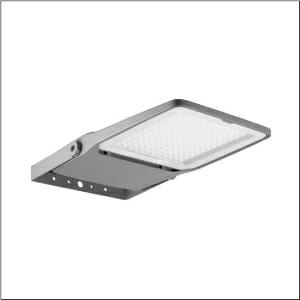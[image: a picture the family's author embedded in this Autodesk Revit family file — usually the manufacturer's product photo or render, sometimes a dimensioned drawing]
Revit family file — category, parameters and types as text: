
# Revit family: floodlight_fl_20_midi___rs17_5xa7682d2b2ac_2315
name_source: partatom
category: Lighting Fixtures
units: mm (PartAtom-declared; Revit-internal decimal feet)

## family parameters
Cut with Voids When Loaded = No
Host = Face
Light Source = No
Part Type = Normal
Room Calculation Point = No
Round Connector Dimension = Use Diameter
Shared = No

## types (1)
- --- (1 x LED 4000K / CRI = 70 (unbekannt), 19540 lm, 4000K)
    Apparent Load = 142 VA
    CIE Flux Codes = 79 92 99 100 100
    Color Rendering = 70
    Color Temperature = 4000K
    Default Elevation = 1800 mm
    Description = Floodlight FL 20 midi, floodlight, primary light control with lens, of plastic, primary optical cover: protective disc, of toughened safety glass, transparent, light distribution: RS17, light emission: direct distribution, primary light characteristic: rotationally symmetric, installation type: surface-mounted, LED, High Power LED, rated luminous flux: 19.540lm, luminous efficacy: 138lm/W, light colour: 740, colour temperature: 4000K, control gear: ECG Plus, control: flexible luminous flux parameterisation, time-dependent luminous flux control, digital communication interface, power reduction, overheat protection, electronic power reduction, with terminal, 5-pole, max. 2.5mm², mains connection: 220..240V, AC, 50/60Hz, rated input power: 142W, LED unit, of diecast aluminium, powder-coated, Siteco® metallic grey (DB 702S), corrosivity category C5 mid according to DIN EN ISO 12944, incl. 1x M20 cable gland for cable Ø 6.5..12mm, length: 731mm, width: 450mm, height: 76mm, housing frame, of diecast aluminium, powder-coated, Siteco® metallic grey (DB 702S), wall fastening, of steel, powder-coated, Siteco® metallic grey (DB 702S), DALI, protection rating (complete): IP66, insulation class (complete): insulation class II (safety insulation), certification: CE, ENEC, VDE, protection symbol: D, permissible operating ambient temperature: -40..+40°C, permissible operating ambient temperature for outdoor applications: -40..+50°C, standard: DIN EN 12944, packaging unit: 1 piece

Light Distribution: RS17
    Height = 76 mm
    Lamp = 1 x LED 4000K / CRI >= 70 (unbekannt)
    Lamp Light Flux = 19540 lm
    Lamp count = 1
    Length = 731 mm
    Luminous efficacy = 138 lm/W
    Manufacturer = Siteco
    ModVariant = No
    Model = 5XA7682D2B2AC
    Mounting Place = Wall
    Mounting Type = Surface mounted
    Number of Poles = 1
    OnlyDefault = Yes
    Power Factor = 1
    Product Name = Floodlight FL 20 midi | RS17
    Product group = floodlight | wall mounted
    ProductGroupID = 2001
    Protection Class = Protection class II
    Protection Degree = IP 66
    RLX_Detail_Level = 1
    RLX_Emergency_Light_Flux = 0 lm
    RLX_Emergency_Type = 0
    RLX_Emergency_Type_DB = No
    RlxData = <blob elided: 86661 chars, md5=67156098>
    Socket = socket
    Standby Power = 0 W
    System Light Flux = 19540 lm
    System Power = 142 W
    Type Comments = factory setting: luminous flux: 100 % | dim-lin: 254 | 489 mA
    Type Image = l_1005944.jpg
    URL = http://relux.com
    VarID = @adj_146629
    Voltage = 0 V
    Weight = 0.00 kg
    Width = 450 mm

## geometry (parser evidence)
native form markers: Blend x4, Sweep x12
no freeform markers — native parametric forms only
